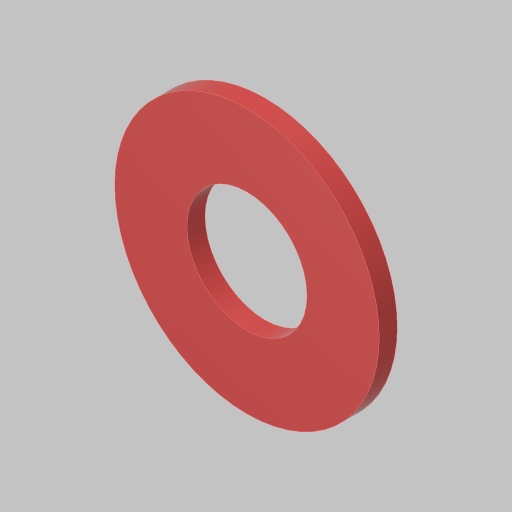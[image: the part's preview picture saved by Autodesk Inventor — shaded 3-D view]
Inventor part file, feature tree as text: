
AUTODESK INVENTOR PART (.ipt)
format: ipt  version: 2023.5 (Build 275446000, 446)  size: 97,792 bytes
history: native  units: in
note: dims shown in document units (in); Inventor stores cm internally (conversion verified against a paired STEP export)
features: extrude x1, sketch x1
ambient origin geometry x8: Origin, YZ Plane, XZ Plane, XY Plane, X Axis, Y Axis, Z Axis, Center Point
bodies: Solid1 (feature_tree)
feature tree (2):
  extrude  "Extrusion1"  Depth=0.0625in
  sketch  "Sketch1"  dims[d0=0.25in d1=0.415in d2=0.0625in d3=0.0in]
